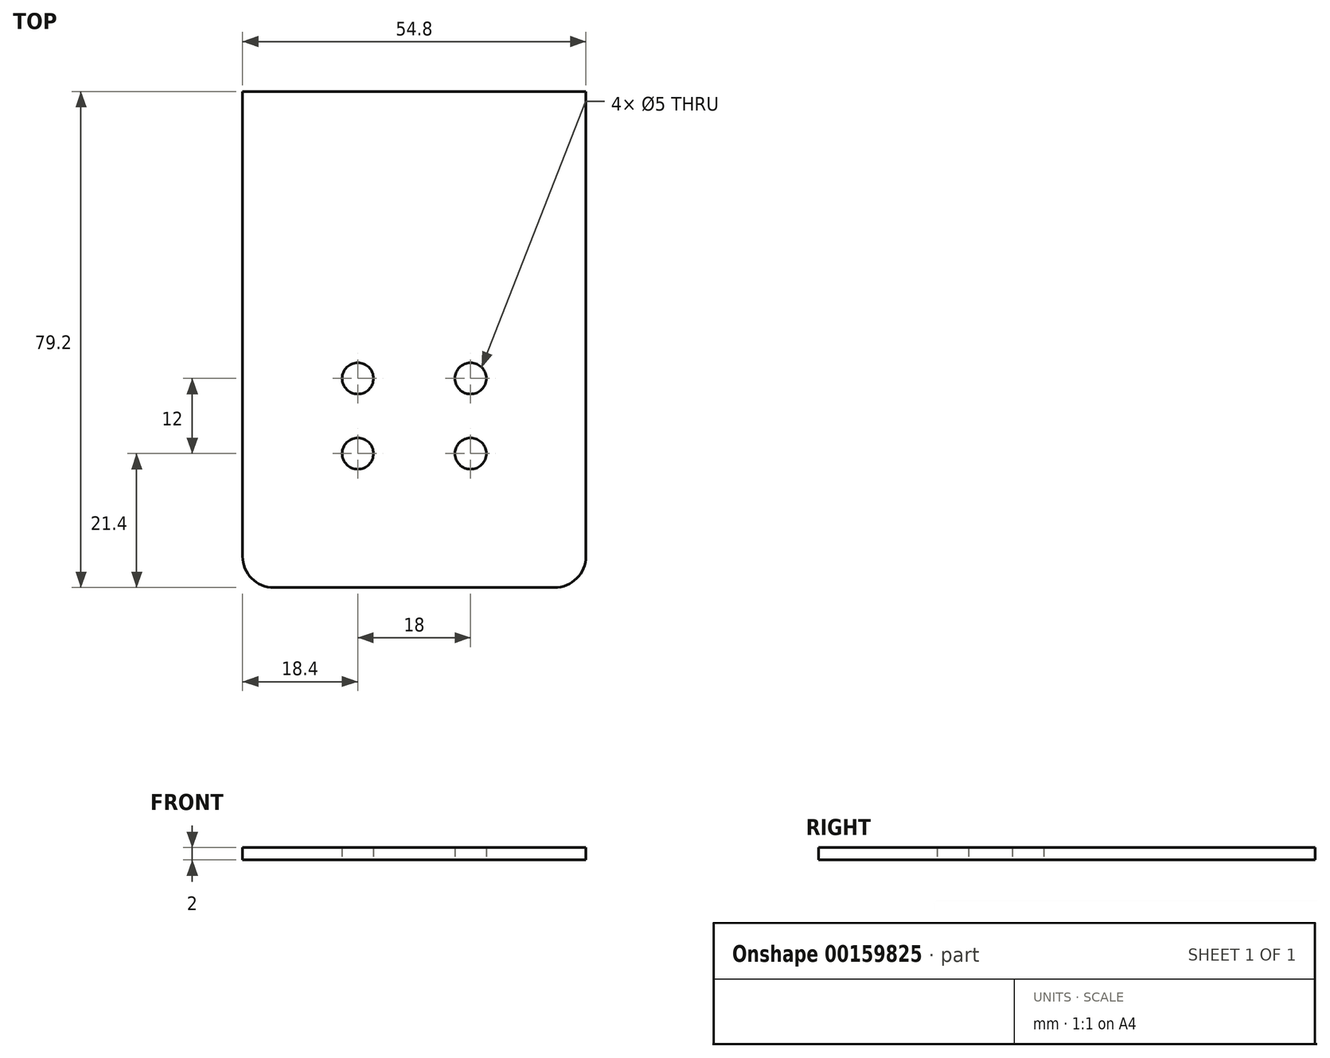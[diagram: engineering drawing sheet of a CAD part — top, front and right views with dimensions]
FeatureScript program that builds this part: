
annotation { "Feature Type Name" : "Feature", "Feature Type Description" : "" }
export const myFeature = defineFeature(function(context is Context, id is Id, definition is map)
    precondition{}
    {
        {
            var Q0;
            Q0=qCreatedBy(makeId("Top.planeOp"),FACE);
            var sketch = newSketch(context, id + "F0", { "sketchPlane" : qUnion([Q0])});
            skLineSegment(sketch, "E0.bottom", {"start": v(0, 0) * mm, "end": v(54.8, 0) * mm});
            skLineSegment(sketch, "E0.top", {"start": v(0, 79.2) * mm, "end": v(54.8, 79.2) * mm});
            skLineSegment(sketch, "E0.left", {"start": v(0, 0) * mm, "end": v(0, 79.2) * mm});
            skLineSegment(sketch, "E0.right", {"start": v(54.8, 0) * mm, "end": v(54.8, 79.2) * mm});
            skCircle(sketch, "E1", {"center": v(18.4, 33.4) * mm, "radius": 2.5 * mm});
            skCircle(sketch, "E2", {"center": v(36.4, 33.4) * mm, "radius": 2.5 * mm});
            skCircle(sketch, "E3", {"center": v(36.4, 21.4) * mm, "radius": 2.5 * mm});
            skCircle(sketch, "E4", {"center": v(18.4, 21.4) * mm, "radius": 2.5 * mm});
            skSolve(sketch);
        }
        {
            var Q0;
            Q0=makeQuery(id+"F0.imprint","IMPRINT",FACE,{"disambiguationData":[TD([[makeQuery(id+"F0.imprint","IMPRINT",EDGE,{"derivedFrom":sQuery(id+"F0.wireOp",EDGE,"E0.bottom")}),1.0]])]});
            extrude(context, id + "F1", {"entities" : qUnion([Q0]), "depth" : 2 * mm});
        }
        {
            var Q0;
            Q0=makeQuery(id+"F1.opExtrude","SWEPT_EDGE",EDGE,{"disambiguationData":[OSD([sQuery(id+"F0.wireOp",EDGE,"E0.bottom"),sQuery(id+"F0.wireOp",EDGE,"E0.right")])]});
            var Q1;
            Q1=makeQuery(id+"F1.opExtrude","SWEPT_EDGE",EDGE,{"disambiguationData":[OSD([sQuery(id+"F0.wireOp",EDGE,"E0.bottom"),sQuery(id+"F0.wireOp",EDGE,"E0.left")])]});
            fillet(context, id + "F2", {"entities" : qUnion([Q0, Q1]), "radius" : 5 * mm, "tangentPropagation" : true, "allowEdgeOverflow" : false});
        }
    });
